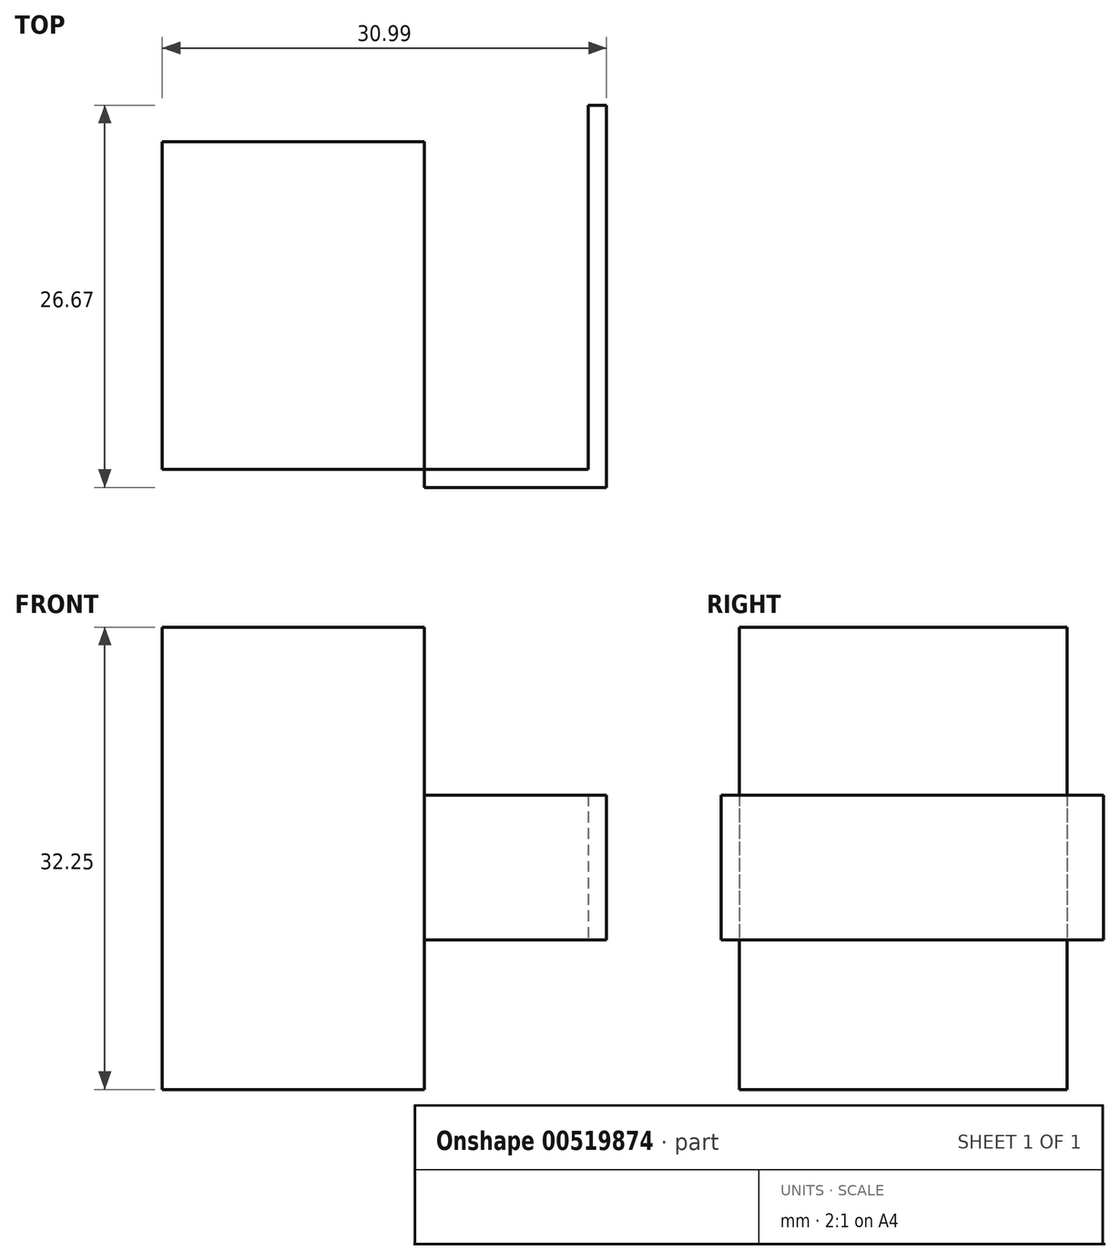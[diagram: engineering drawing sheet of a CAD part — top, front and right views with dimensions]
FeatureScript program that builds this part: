
annotation { "Feature Type Name" : "Feature", "Feature Type Description" : "" }
export const myFeature = defineFeature(function(context is Context, id is Id, definition is map)
    precondition{}
    {
        {
            var Q0;
            Q0=qCreatedBy(makeId("Front.planeOp"),FACE);
            var sketch = newSketch(context, id + "F0", { "sketchPlane" : qUnion([Q0])});
            skLineSegment(sketch, "E0.bottom", {"start": v(0, 7.2) * mm, "end": v(18.29, 7.2) * mm});
            skLineSegment(sketch, "E0.top", {"start": v(0, -25.05) * mm, "end": v(18.29, -25.05) * mm});
            skLineSegment(sketch, "E0.left", {"start": v(0, 7.2) * mm, "end": v(0, -25.05) * mm});
            skLineSegment(sketch, "E0.right", {"start": v(18.29, 7.2) * mm, "end": v(18.29, -25.05) * mm});
            skSolve(sketch);
        }
        {
            var Q0;
            Q0=makeQuery(id+"F0.imprint","IMPRINT",FACE,{"disambiguationData":[TD([[makeQuery(id+"F0.imprint","IMPRINT",EDGE,{"derivedFrom":sQuery(id+"F0.wireOp",EDGE,"E0.bottom")}),-1.0]])]});
            extrude(context, id + "F1", {"entities" : qUnion([Q0]), "depth" : 22.86 * mm, "offsetDistance" : 25.4 * mm});
        }
        {
            var Q0;
            Q0=makeQuery(id+"F1.opExtrude","CAP_FACE",FACE,{"disambiguationData":[OSD([sQuery(id+"F0.wireOp",EDGE,"E0.bottom"),sQuery(id+"F0.wireOp",EDGE,"E0.top"),sQuery(id+"F0.wireOp",EDGE,"E0.left"),sQuery(id+"F0.wireOp",EDGE,"E0.right")])],"isStart":false});
            var sketch = newSketch(context, id + "F2", { "sketchPlane" : qUnion([Q0])});
            skLineSegment(sketch, "E1.bottom", {"start": v(18.29, -4.52) * mm, "end": v(30.99, -4.52) * mm});
            skLineSegment(sketch, "E1.top", {"start": v(18.29, -14.62) * mm, "end": v(30.99, -14.62) * mm});
            skLineSegment(sketch, "E1.left", {"start": v(18.29, -4.52) * mm, "end": v(18.29, -14.62) * mm});
            skLineSegment(sketch, "E1.right", {"start": v(30.99, -4.52) * mm, "end": v(30.99, -14.62) * mm});
            skSolve(sketch);
        }
        {
            var Q0;
            Q0 = qSketchRegion(id + "F2", true);
            extrude(context, id + "F3", {"entities" : qUnion([Q0]), "depth" : 1.27 * mm, "offsetDistance" : 25.4 * mm});
        }
        {
            var Q0;
            Q0=makeQuery(id+"F3.opExtrude","CAP_FACE",FACE,{"disambiguationData":[OSD([sQuery(id+"F2.wireOp",EDGE,"E1.bottom"),sQuery(id+"F2.wireOp",EDGE,"E1.top"),sQuery(id+"F2.wireOp",EDGE,"E1.left"),sQuery(id+"F2.wireOp",EDGE,"E1.right")])],"isStart":true});
            var sketch = newSketch(context, id + "F4", { "sketchPlane" : qUnion([Q0])});
            skLineSegment(sketch, "E2.bottom", {"start": v(-30.99, -4.52) * mm, "end": v(-29.72, -4.52) * mm});
            skLineSegment(sketch, "E2.top", {"start": v(-30.99, -14.62) * mm, "end": v(-29.72, -14.62) * mm});
            skLineSegment(sketch, "E2.left", {"start": v(-30.99, -4.52) * mm, "end": v(-30.99, -14.62) * mm});
            skLineSegment(sketch, "E2.right", {"start": v(-29.72, -4.52) * mm, "end": v(-29.72, -14.62) * mm});
            skSolve(sketch);
        }
        {
            var Q0;
            Q0 = qSketchRegion(id + "F4", true);
            extrude(context, id + "F5", {"entities" : qUnion([Q0]), "operationType" : NewBodyOperationType.ADD, "depth" : 25.4 * mm, "offsetDistance" : 25.4 * mm});
        }
    });
